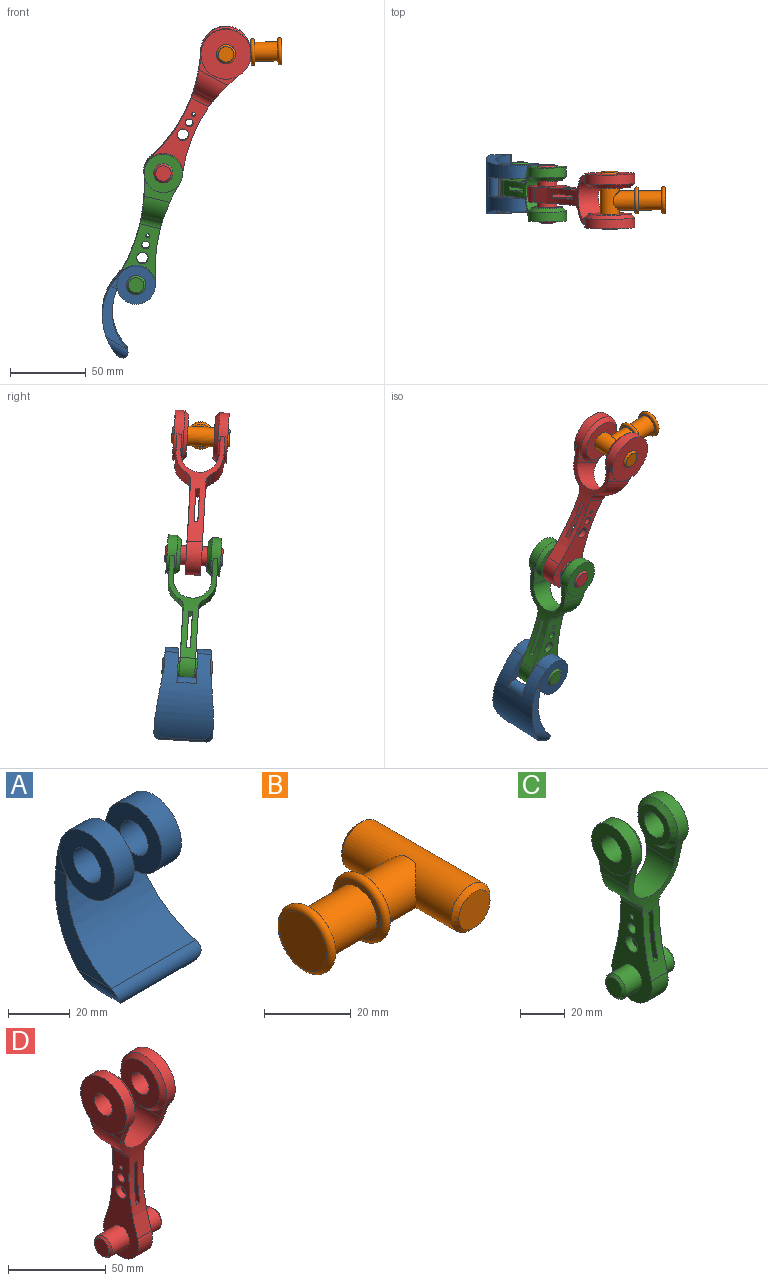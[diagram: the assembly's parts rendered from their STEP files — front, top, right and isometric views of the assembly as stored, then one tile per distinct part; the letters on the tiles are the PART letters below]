
ASSEMBLY  parts=4 mates=3
PART A: 19 faces, bbox 39.3x32.7x59.8 mm
  f0: cylinder r=35.56mm len=38.7mm, axis (-1,0,0), area 1425.8mm2, adj f2,f3,f5,f9,f10,f11,f12,f16
  f1: cylinder r=39.21mm len=51.08mm, axis (-1,0,0), area 1807.4mm2, adj f3,f5,f9,f10,f11,f12,f13,f14
  f2: cylinder r=3.81mm len=38.83mm, axis (-1,0,0), area 347.3mm2, adj f0,f12,f13,f14,f15,f16
  f3: cylinder r=12.7mm len=25.4mm, axis (-1,0,0), area 587.1mm2, adj f0,f1,f8,f10
  f4: cylinder r=6.35mm len=12.7mm, axis (-1,0,0), area 354.7mm2, adj f8,f10
  f5: cylinder r=12.7mm len=25.4mm, axis (-1,0,0), area 587mm2, adj f0,f1,f7,f9
  f6: cylinder r=6.35mm len=12.7mm, axis (-1,0,0), area 354.7mm2, adj f7,f9
  f7: plane 25.53x25.52mm, normal (1,0,0), area 380mm2, adj f5,f6,f16,f18
  f8: plane 25.53x25.51mm, normal (-1,0,0), area 380mm2, adj f3,f4,f17
  f9: plane 31.7x27.07mm, normal (-1,0,0), area 430.2mm2, adj f0,f1,f5,f6,f11
  f10: plane 31.7x27.07mm, normal (1,0,0), area 430.2mm2, adj f0,f1,f3,f4,f11
  f11: cylinder r=5.08mm len=12.7mm, axis (1,0,0), area 109.3mm2, adj f0,f1,f9,f10
  f12: plane 31.19x30.26mm, normal (-0.99,0,0.13), area 244.2mm2, adj f0,f1,f2,f13,f17
  f13: cylinder r=6.35mm len=18.11mm, axis (0,1,0), area 113.9mm2, adj f1,f2,f12,f14
  f14: plane 26.13x2.31mm, normal (0,0,-1), area 60.4mm2, adj f1,f2,f13,f15
  f15: cylinder r=6.35mm len=18.11mm, axis (0,1,0), area 113.8mm2, adj f1,f2,f14,f16
  f16: plane 31.51x30.28mm, normal (0.99,0,0.13), area 245.9mm2, adj f0,f1,f2,f7,f15,f18
  f17: plane 13.14x4.9mm, normal (-1,0,0), area 21.3mm2, adj f0,f1,f8,f12
  f18: plane 12.87x4.87mm, normal (1,0,0), area 19.8mm2, adj f1,f7,f16
PART B: 15 faces, bbox 43.2x38.1x19.2 mm
  f0: cylinder r=6.35mm len=15.24mm, axis (-1,0,0), area 608mm2, adj f2,f5
  f1: plane 15.24x15.24mm, normal (-1,0,0), area 182.4mm2, adj f3
  f2: plane 15.24x15.24mm, normal (1,0,0), area 55.7mm2, adj f0,f3
  f3: torus R=7.62mm, axis (-1,0,0), area 211.3mm2, adj f1,f2
  f4: plane 15.24x15.24mm, normal (1,0,0), area 55.7mm2, adj f6,f10
  f5: plane 15.24x15.24mm, normal (-1,0,0), area 55.7mm2, adj f0,f6
  f6: torus R=7.62mm, axis (1,0,0), area 211.3mm2, adj f4,f5
  f7: cylinder r=6.35mm len=35.56mm, axis (0,1,0), area 1269.6mm2, adj f10,f11,f12,f13,f14
  f8: plane 10.16x10.16mm, normal (0,-1,0), area 81.1mm2, adj f14
  f9: plane 10.16x10.16mm, normal (0,1,0), area 81.1mm2, adj f13
  f10: cylinder r=6.35mm len=14.1mm, axis (-1,0,0), area 485.6mm2, adj f4,f7,f11,f12
  f11: plane 4.83x0.48mm, normal (1,0,0), area 1.5mm2, adj f7,f10
  f12: plane 4.83x0.48mm, normal (1,0,0), area 1.5mm2, adj f7,f10
  f13: cone r=6.35mm half-angle=45deg, axis (0,-1,0), area 64.5mm2, adj f7,f9
  f14: cone r=5.08mm half-angle=45deg, axis (0,1,0), area 64.5mm2, adj f7,f8
PART C: 40 faces, bbox 35.6x25.4x101.6 mm
  f0: cylinder r=114.3mm len=68.58mm, axis (-1,0,0), area 576.9mm2, adj f2,f3,f4,f5,f6,f7,f9,f10
  f1: cylinder r=114.3mm len=68.58mm, axis (-1,0,0), area 577mm2, adj f2,f3,f4,f5,f6,f7,f9,f10
  f2: cylinder r=15.88mm len=17.34mm, axis (0,-1,0), area 250.3mm2, adj f0,f1,f3,f9
  f3: cylinder r=6.35mm len=14.09mm, axis (0,-1,0), area 91mm2, adj f0,f1,f2,f10
  f4: cylinder r=6.35mm len=14.09mm, axis (0,-1,0), area 91mm2, adj f0,f1,f5,f11
  f5: cylinder r=15.88mm len=17.34mm, axis (0,-1,0), area 250.3mm2, adj f0,f1,f4,f12
  f6: cylinder r=12.7mm len=25.4mm, axis (0,-1,0), area 604.5mm2, adj f0,f1,f13,f14
  f7: cylinder r=12.7mm len=25.4mm, axis (-1,0,0), area 404.3mm2, adj f0,f1,f12,f13,f17,f22
  f8: cylinder r=6.35mm len=12.7mm, axis (1,0,0), area 354.7mm2, adj f17,f19
  f9: plane 24.23x13.97mm, normal (1,0,0), area 128mm2, adj f0,f1,f2,f15
  f10: plane 52.05x25.4mm, normal (1,0,0), area 757.2mm2, adj f0,f1,f3,f25,f29,f34,f35,f36
  f11: plane 52.05x25.4mm, normal (-1,0,0), area 757.2mm2, adj f0,f1,f4,f24,f29,f37,f38,f39
  f12: plane 24.23x13.97mm, normal (-1,0,0), area 128mm2, adj f0,f1,f5,f7
  f13: plane 24.23x13.97mm, normal (1,0,0), area 128mm2, adj f0,f1,f6,f7
  f14: plane 24.23x13.97mm, normal (-1,0,0), area 128mm2, adj f0,f1,f6,f15
  f15: cylinder r=12.7mm len=25.4mm, axis (-1,0,0), area 404.3mm2, adj f0,f1,f9,f14,f16,f21
  f16: plane 25.4x25.4mm, normal (1,0,0), area 380mm2, adj f15,f18
  f17: plane 25.4x25.4mm, normal (-1,0,0), area 380mm2, adj f7,f8
  f18: cylinder r=6.35mm len=12.7mm, axis (1,0,0), area 354.7mm2, adj f16,f20
  f19: plane 20.32x20.32mm, normal (1,0,0), area 197.6mm2, adj f8,f22
  f20: plane 20.32x20.32mm, normal (-1,0,0), area 197.6mm2, adj f18,f21
  f21: cone r=12.7mm half-angle=45deg, axis (1,0,0), area 258mm2, adj f15,f20
  f22: cone r=10.16mm half-angle=45deg, axis (-1,0,0), area 258mm2, adj f7,f19
  f23: plane 10.16x10.16mm, normal (-1,0,0), area 81.1mm2, adj f28
  f24: cylinder r=6.35mm len=12.7mm, axis (-1,0,0), area 405.4mm2, adj f11,f28
  f25: cylinder r=6.35mm len=12.7mm, axis (-1,0,0), area 405.4mm2, adj f10,f27
  f26: plane 10.16x10.16mm, normal (1,0,0), area 81.1mm2, adj f27
  f27: cone r=5.08mm half-angle=45deg, axis (-1,0,0), area 64.5mm2, adj f25,f26
  f28: cone r=6.35mm half-angle=45deg, axis (1,0,0), area 64.5mm2, adj f23,f24
  f29: cylinder r=12.7mm len=25.4mm, axis (-1,0,0), area 484mm2, adj f0,f1,f10,f11
  f30: plane 20.02x2.54mm, normal (0,0,1), area 50.9mm2, adj f0,f1,f31,f33
  f31: plane 25.4x20.02mm, normal (1,0,0), area 333mm2, adj f0,f1,f30,f32,f37,f38,f39
  f32: plane 13.72x2.54mm, normal (0,0,-1), area 34.8mm2, adj f0,f1,f31,f33
  f33: plane 25.4x20.02mm, normal (-1,0,0), area 333mm2, adj f0,f1,f30,f32,f34,f35,f36
  f34: cylinder r=1.27mm len=3.81mm, axis (1,0,0), area 30.4mm2, adj f10,f33
  f35: cylinder r=2.54mm len=5.08mm, axis (1,0,0), area 60.8mm2, adj f10,f33
  f36: cylinder r=3.81mm len=7.62mm, axis (1,0,0), area 91.2mm2, adj f10,f33
  f37: cylinder r=1.27mm len=3.81mm, axis (1,0,0), area 30.4mm2, adj f11,f31
  f38: cylinder r=2.54mm len=5.08mm, axis (1,0,0), area 60.8mm2, adj f11,f31
  f39: cylinder r=3.81mm len=7.62mm, axis (1,0,0), area 91.2mm2, adj f11,f31
PART D: 40 faces, bbox 38.1x33x118.1 mm
  f0: cylinder r=101.6mm len=77.6mm, axis (-1,0,0), area 688.9mm2, adj f2,f3,f4,f5,f6,f7,f9,f10
  f1: cylinder r=101.6mm len=77.61mm, axis (-1,0,0), area 689.2mm2, adj f2,f3,f4,f5,f6,f7,f9,f10
  f2: cylinder r=15.88mm len=21.45mm, axis (0,-1,0), area 283.9mm2, adj f0,f1,f3,f9
  f3: cylinder r=6.35mm len=14.56mm, axis (0,-1,0), area 89.9mm2, adj f0,f1,f2,f10
  f4: cylinder r=6.35mm len=14.56mm, axis (0,-1,0), area 89.9mm2, adj f0,f1,f5,f11
  f5: cylinder r=15.88mm len=21.45mm, axis (0,-1,0), area 283.9mm2, adj f0,f1,f4,f12
  f6: cylinder r=12.7mm len=25.4mm, axis (0,-1,0), area 680mm2, adj f0,f1,f13,f14
  f7: cylinder r=16.51mm len=33.02mm, axis (-1,0,0), area 539mm2, adj f0,f1,f12,f13,f17,f22
  f8: cylinder r=6.35mm len=12.7mm, axis (1,0,0), area 354.7mm2, adj f17,f19
  f9: plane 29.99x10.87mm, normal (1,0,0), area 70.1mm2, adj f0,f1,f2,f15
  f10: plane 64.75x25.4mm, normal (1,0,0), area 856.2mm2, adj f0,f1,f3,f25,f29,f34,f35,f36
  f11: plane 64.75x25.4mm, normal (-1,0,0), area 856.2mm2, adj f0,f1,f4,f24,f29,f37,f38,f39
  f12: plane 29.99x10.87mm, normal (-1,0,0), area 70.1mm2, adj f0,f1,f5,f7
  f13: plane 29.99x10.87mm, normal (1,0,0), area 70.1mm2, adj f0,f1,f6,f7
  f14: plane 29.99x10.87mm, normal (-1,0,0), area 70.1mm2, adj f0,f1,f6,f15
  f15: cylinder r=16.51mm len=33.02mm, axis (-1,0,0), area 539mm2, adj f0,f1,f9,f14,f16,f21
  f16: plane 33.02x33.02mm, normal (1,0,0), area 729.7mm2, adj f15,f18
  f17: plane 33.02x33.02mm, normal (-1,0,0), area 729.7mm2, adj f7,f8
  f18: cylinder r=6.35mm len=12.7mm, axis (1,0,0), area 354.7mm2, adj f16,f20
  f19: plane 27.94x27.94mm, normal (1,0,0), area 486.4mm2, adj f8,f22
  f20: plane 27.94x27.94mm, normal (-1,0,0), area 486.4mm2, adj f18,f21
  f21: cone r=16.51mm half-angle=45deg, axis (1,0,0), area 344mm2, adj f15,f20
  f22: cone r=13.97mm half-angle=45deg, axis (-1,0,0), area 344mm2, adj f7,f19
  f23: plane 10.16x10.16mm, normal (-1,0,0), area 81.1mm2, adj f28
  f24: cylinder r=6.35mm len=12.7mm, axis (-1,0,0), area 506.7mm2, adj f11,f28
  f25: cylinder r=6.35mm len=12.7mm, axis (-1,0,0), area 506.7mm2, adj f10,f27
  f26: plane 10.16x10.16mm, normal (1,0,0), area 81.1mm2, adj f27
  f27: cone r=5.08mm half-angle=45deg, axis (-1,0,0), area 64.5mm2, adj f25,f26
  f28: cone r=6.35mm half-angle=45deg, axis (1,0,0), area 64.5mm2, adj f23,f24
  f29: cylinder r=12.7mm len=25.4mm, axis (-1,0,0), area 496.4mm2, adj f0,f1,f10,f11
  f30: plane 14.52x2.54mm, normal (0,0,1), area 36.9mm2, adj f0,f1,f31,f33
  f31: plane 25.4x14.52mm, normal (1,0,0), area 237.3mm2, adj f0,f1,f30,f32,f37,f38,f39
  f32: plane 11.89x2.54mm, normal (0,0,-1), area 30.2mm2, adj f0,f1,f31,f33
  f33: plane 25.4x14.52mm, normal (-1,0,0), area 237.3mm2, adj f0,f1,f30,f32,f34,f35,f36
  f34: cylinder r=1.27mm len=3.81mm, axis (1,0,0), area 30.4mm2, adj f10,f33
  f35: cylinder r=2.54mm len=5.08mm, axis (1,0,0), area 60.8mm2, adj f10,f33
  f36: cylinder r=3.81mm len=7.62mm, axis (1,0,0), area 91.2mm2, adj f10,f33
  f37: cylinder r=1.27mm len=3.81mm, axis (1,0,0), area 30.4mm2, adj f11,f31
  f38: cylinder r=2.54mm len=5.08mm, axis (1,0,0), area 60.8mm2, adj f11,f31
  f39: cylinder r=3.81mm len=7.62mm, axis (1,0,0), area 91.2mm2, adj f11,f31
PLACE A rot(axis=(0.27,0.22,0.94),95deg) t=(44.12,32.87,-90.82)mm
PLACE B rot(axis=(0,1,0.03),178.6deg) t=(122.39,24.01,62.18)mm fixed
PLACE C rot(axis=(0.15,0.09,0.99),91.6deg) t=(62.06,28.47,-16.89)mm
PLACE D rot(axis=(0.26,0.2,0.94),94.4deg) t=(103.35,23.93,61.71)mm
MATE revolute B.f7 <-> D.f7  axis (0.01,-1,-0.06) through (103.45,6.18,60.63)mm
MATE revolute D.f24 <-> C.f7  axis (-0.01,1,0.06) through (62.15,10.73,-17.97)mm
MATE revolute C.f24 <-> A.f3  axis (0.01,-1,-0.06) through (44.15,27.8,-91.13)mm
